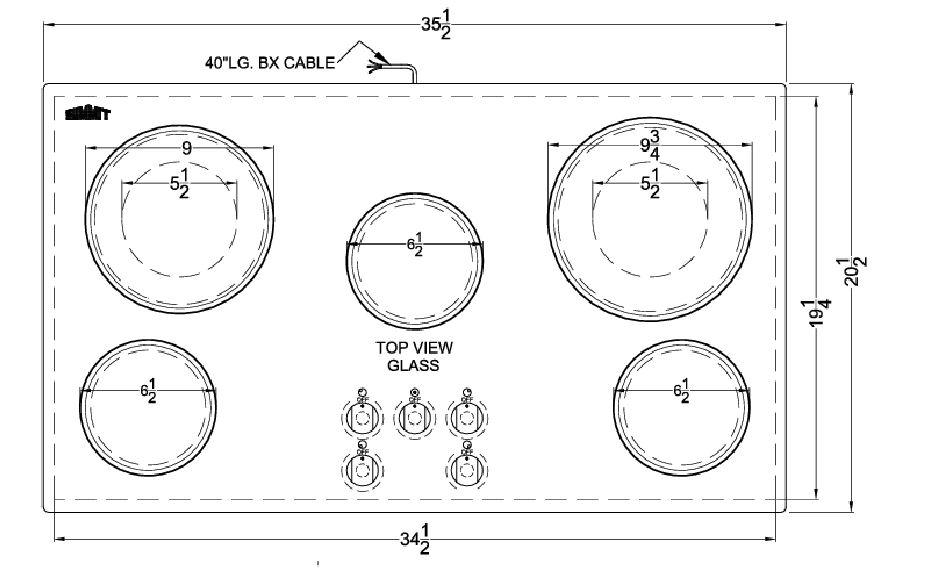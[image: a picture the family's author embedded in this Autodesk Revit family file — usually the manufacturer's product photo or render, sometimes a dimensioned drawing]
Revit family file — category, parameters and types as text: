
# Revit family: QF_Summit_CR5B36MB_Electric Cooktop
name_source: partatom
category: Specialty Equipment
units: mm (PartAtom-declared; Revit-internal decimal feet)

## family parameters
Always vertical = Yes
Cut with Voids When Loaded = No
Part Type = Normal
Room Calculation Point = No
Round Connector Dimension = Use Diameter
Shared = No
Work Plane-Based = No

## types (1)
- QF_Summit_CR5B36MB_Electric Cooktop
    Apparent Power = 7200 VA
    Conn Conduit = Yes
    Cycle = 60 Hz
    Default Elevation = 0"
    Depth = 20 1/2"
    Description = Electric Cooktop
    Elec Conn Connection Height = 0"
    Elec Conn RI Height = 0"
    FL Amps = 30 A
    Foodservice Equipment Identifier = Yes
    Height = 2 1/8"
    Identify Quantity as Lot = Yes
    Length = 35 1/2"
    Manufacturer = Summit
    Max Overcurrent Protection = 0 A
    Min Ckt Ampacity = 0 A
    Model = CR5B36MB
    Number of Poles = 1
    Phase = 1
    Volts = 240 V
    Watts = 7200 W
    Weight in Pounds = 36

## geometry (parser evidence)
native form markers: Sweep x3
no freeform markers — native parametric forms only
